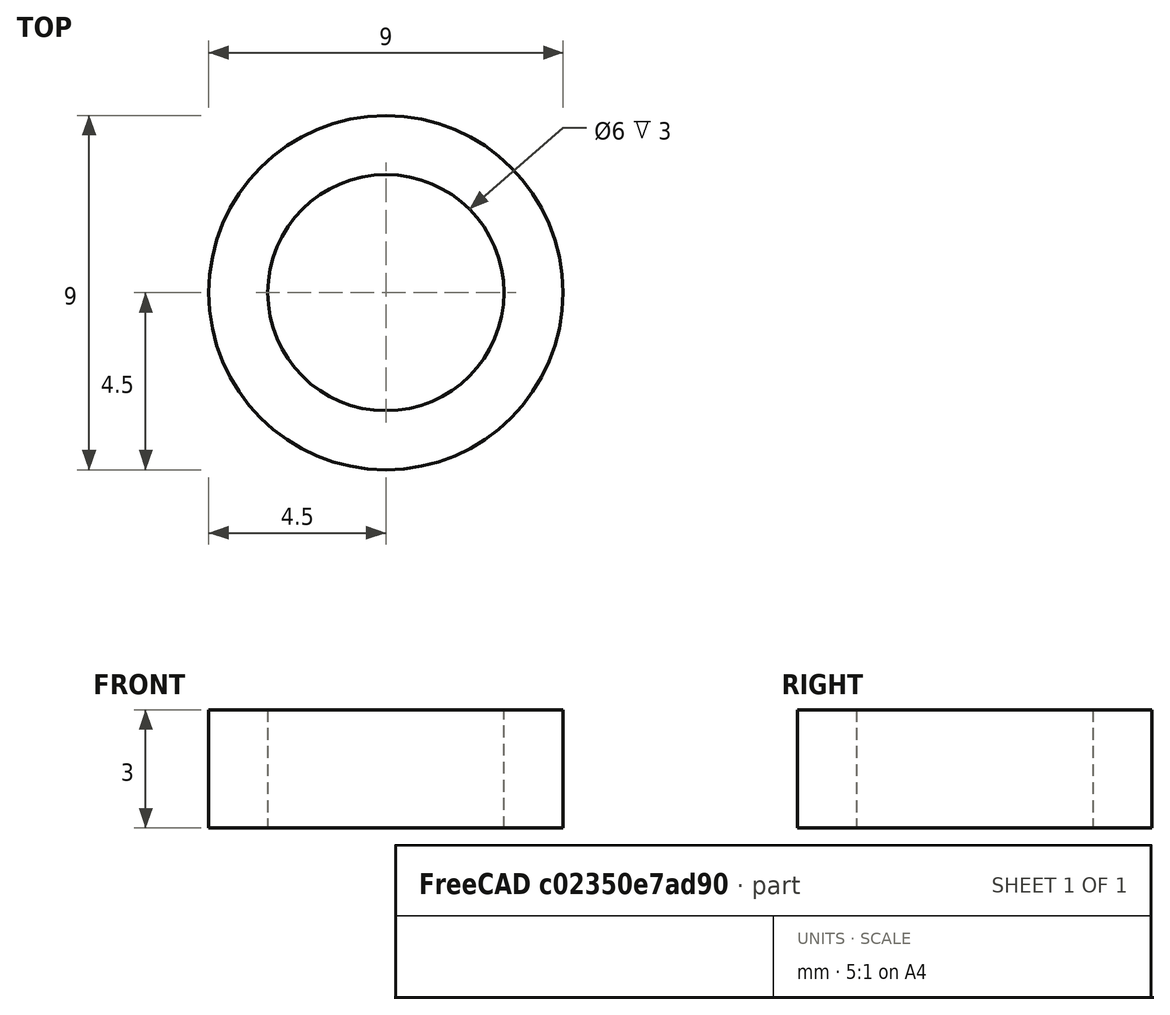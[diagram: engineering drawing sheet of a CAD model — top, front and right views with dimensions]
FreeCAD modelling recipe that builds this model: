
FCSTD DOCUMENT  (FreeCAD 0.21R33668 +26 (Git))
Label: mag_NOR099
License: All rights reserved
LicenseURL: http://en.wikipedia.org/wiki/All_rights_reserved
objects: Sketcher::SketchObject×1, PartDesign::Pad×1, PartDesign::Body×1
note: 4 computed .brp shape members not serialized (recipe doc carries the construction recipe); baked Part::Feature solids carry a one-line shape summary decoded from their .brp

FEATURE [Sketcher::SketchObject] Sketch
  FullyConstrained = true
  MapMode = 5
  Support = -> [XY_Plane]
  sketch-geometry (2):
    g0: Circle CenterX=0 CenterY=0 CenterZ=0 NormalX=0 NormalY=0 NormalZ=1 AngleXU=0 Radius=3
    g1: Circle CenterX=0 CenterY=0 CenterZ=0 NormalX=0 NormalY=0 NormalZ=1 AngleXU=0 Radius=4.5
  constraints (4):
    c: Coincident(g0,g-1)
    c: Diameter(g0) = 6
    c: Coincident(g1,g0)
    c: Diameter(g1) = 9
FEATURE [PartDesign::Pad] Pad
  Direction = (0,0,1)
  Length = 3
  Length2 = 10
  Profile = -> Sketch
  ReferenceAxis = -> Sketch [N_Axis]
  Type = 0
FEATURE [PartDesign::Body] Body
  Group = -> [Sketch,Pad]
  Origin = -> Origin
  Tip = -> Pad
